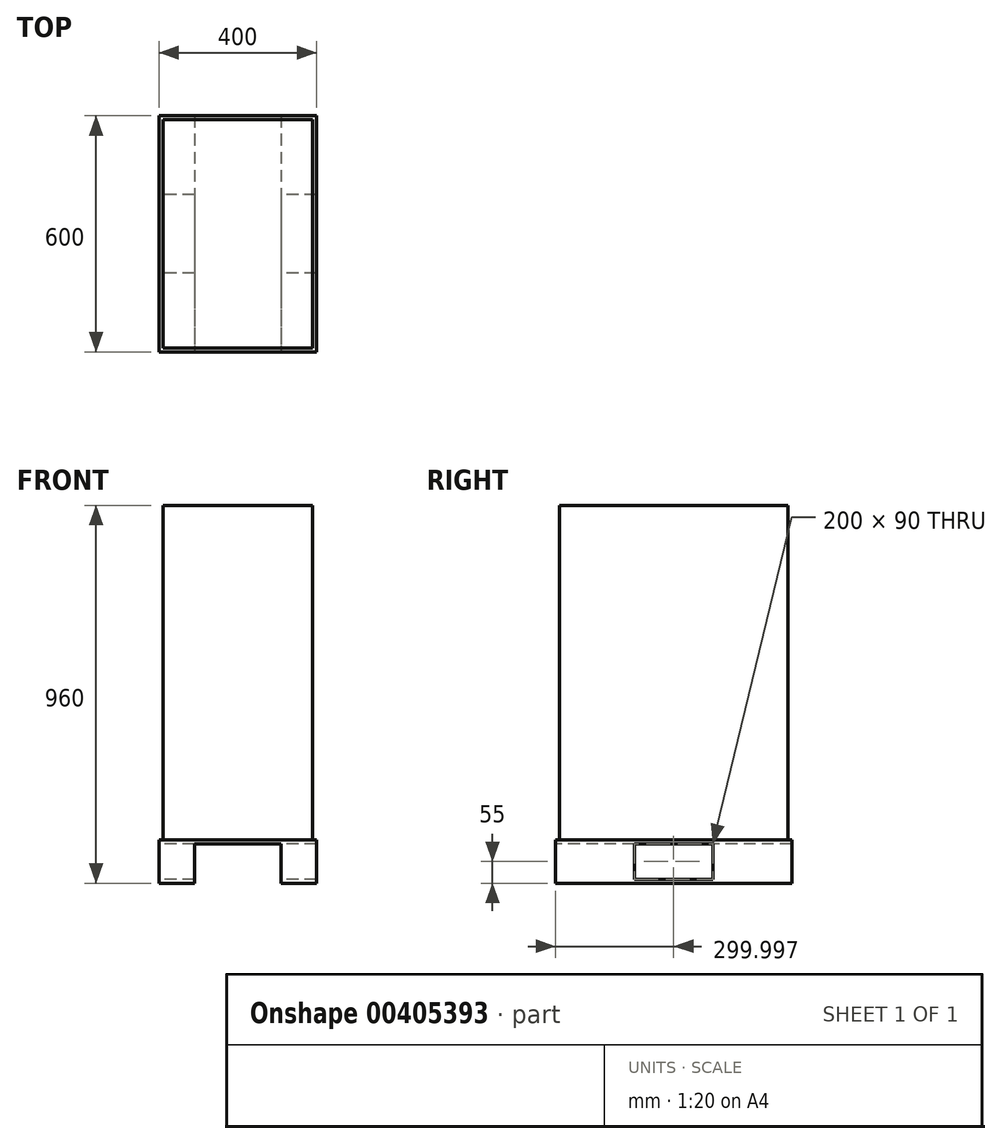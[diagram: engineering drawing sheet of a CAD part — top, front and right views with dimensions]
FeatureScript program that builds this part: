
annotation { "Feature Type Name" : "Feature", "Feature Type Description" : "" }
export const myFeature = defineFeature(function(context is Context, id is Id, definition is map)
    precondition{}
    {
        {
            var Q0;
            Q0=qCreatedBy(makeId("Top.planeOp"),FACE);
            var sketch = newSketch(context, id + "F0", { "sketchPlane" : qUnion([Q0])});
            skLineSegment(sketch, "E0.bottom", {"start": v(-245.66, 395.7) * mm, "end": v(154.34, 395.7) * mm});
            skLineSegment(sketch, "E0.top", {"start": v(-245.66, -204.3) * mm, "end": v(154.34, -204.3) * mm});
            skLineSegment(sketch, "E0.left", {"start": v(-245.66, 395.7) * mm, "end": v(-245.66, -204.3) * mm});
            skLineSegment(sketch, "E0.right", {"start": v(154.34, 395.7) * mm, "end": v(154.34, -204.3) * mm});
            skSolve(sketch);
        }
        {
            var Q0;
            Q0=makeQuery(id+"F0.imprint","IMPRINT",FACE,{"disambiguationData":[TD([[makeQuery(id+"F0.imprint","IMPRINT",EDGE,{"derivedFrom":sQuery(id+"F0.wireOp",EDGE,"E0.bottom")}),-1.0]])]});
            extrude(context, id + "F1", {"entities" : qUnion([Q0]), "depth" : 110 * mm});
        }
        {
            var Q0;
            Q0=makeQuery(id+"F1.opExtrude","SWEPT_FACE",FACE,{"disambiguationData":[OSD([sQuery(id+"F0.wireOp",EDGE,"E0.top")])]});
            var sketch = newSketch(context, id + "F2", { "sketchPlane" : qUnion([Q0])});
            skLineSegment(sketch, "E1.bottom", {"start": v(-155.66, 100) * mm, "end": v(64.34, 100) * mm});
            skLineSegment(sketch, "E1.top", {"start": v(-155.66, -177.98) * mm, "end": v(64.34, -177.98) * mm});
            skLineSegment(sketch, "E1.left", {"start": v(-155.66, 100) * mm, "end": v(-155.66, -177.98) * mm});
            skLineSegment(sketch, "E1.right", {"start": v(64.34, 100) * mm, "end": v(64.34, -177.98) * mm});
            skSolve(sketch);
        }
        {
            var Q0;
            {var subQ0=sQuery(id+"F2.wireOp",EDGE,"E1.bottom");Q0=makeQuery(id+"F2.imprint","IMPRINT",FACE,{"disambiguationData":[TD([[makeQuery(id+"F2.imprint","IMPRINT",EDGE,{"derivedFrom":subQ0}),-1.0]])]});}
            var Q1;
            {var subQ0=sQuery(id+"F2.wireOp",EDGE,"E1.top");Q1=makeQuery(id+"F2.imprint","IMPRINT",FACE,{"disambiguationData":[TD([[makeQuery(id+"F2.imprint","IMPRINT",EDGE,{"derivedFrom":subQ0}),1.0]])]});}
            extrude(context, id + "F3", {"entities" : qUnion([Q0, Q1]), "operationType" : NewBodyOperationType.REMOVE, "endBound" : BoundingType.THROUGH_ALL, "oppositeDirection" : true, "depth" : 25 * mm});
        }
        {
            var Q0;
            Q0=makeQuery(id+"F1.opExtrude","SWEPT_FACE",FACE,{"disambiguationData":[OSD([sQuery(id+"F0.wireOp",EDGE,"E0.left")])]});
            var sketch = newSketch(context, id + "F4", { "sketchPlane" : qUnion([Q0])});
            skLineSegment(sketch, "E2.bottom", {"start": v(-195.7, 100) * mm, "end": v(4.3, 100) * mm});
            skLineSegment(sketch, "E2.top", {"start": v(-195.7, 10) * mm, "end": v(4.3, 10) * mm});
            skLineSegment(sketch, "E2.left", {"start": v(-195.7, 100) * mm, "end": v(-195.7, 10) * mm});
            skLineSegment(sketch, "E2.right", {"start": v(4.3, 100) * mm, "end": v(4.3, 10) * mm});
            skSolve(sketch);
        }
        {
            var Q0;
            Q0=makeQuery(id+"F4.imprint","IMPRINT",FACE,{"disambiguationData":[TD([[makeQuery(id+"F4.imprint","IMPRINT",EDGE,{"derivedFrom":sQuery(id+"F4.wireOp",EDGE,"E2.bottom")}),-1.0]])]});
            extrude(context, id + "F5", {"entities" : qUnion([Q0]), "operationType" : NewBodyOperationType.REMOVE, "oppositeDirection" : true, "depth" : 401 * mm});
        }
        {
            var Q0;
            Q0=makeQuery(id+"F1.opExtrude","CAP_FACE",FACE,{"disambiguationData":[OSD([sQuery(id+"F0.wireOp",EDGE,"E0.bottom"),sQuery(id+"F0.wireOp",EDGE,"E0.top"),sQuery(id+"F0.wireOp",EDGE,"E0.left"),sQuery(id+"F0.wireOp",EDGE,"E0.right")])],"isStart":false});
            var sketch = newSketch(context, id + "F6", { "sketchPlane" : qUnion([Q0])});
            skLineSegment(sketch, "E3.bottom", {"start": v(-235.66, 385.7) * mm, "end": v(144.34, 385.7) * mm});
            skLineSegment(sketch, "E3.top", {"start": v(-235.66, -194.3) * mm, "end": v(144.34, -194.3) * mm});
            skLineSegment(sketch, "E3.left", {"start": v(-235.66, 385.7) * mm, "end": v(-235.66, -194.3) * mm});
            skLineSegment(sketch, "E3.right", {"start": v(144.34, 385.7) * mm, "end": v(144.34, -194.3) * mm});
            skSolve(sketch);
        }
        {
            var Q0;
            Q0=makeQuery(id+"F6.imprint","IMPRINT",FACE,{"disambiguationData":[TD([[makeQuery(id+"F6.imprint","IMPRINT",EDGE,{"derivedFrom":sQuery(id+"F6.wireOp",EDGE,"E3.bottom")}),-1.0]])]});
            extrude(context, id + "F7", {"entities" : qUnion([Q0]), "operationType" : NewBodyOperationType.ADD, "depth" : 850 * mm});
        }
    });
